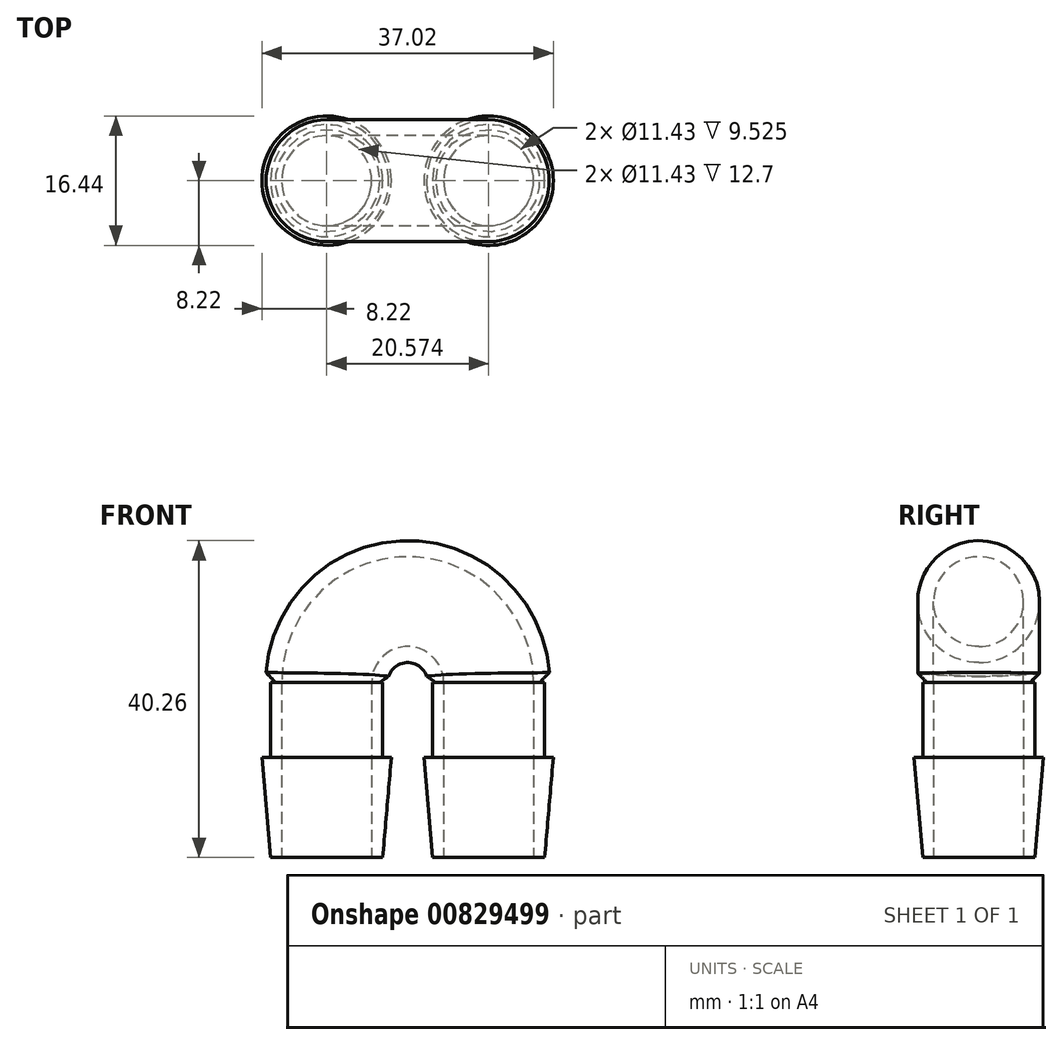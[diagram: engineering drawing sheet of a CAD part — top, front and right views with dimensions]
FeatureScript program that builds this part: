
annotation { "Feature Type Name" : "Feature", "Feature Type Description" : "" }
export const myFeature = defineFeature(function(context is Context, id is Id, definition is map)
    precondition{}
    {
        {
            var Q0;
            Q0=qCreatedBy(makeId("Top.planeOp"),FACE);
            var sketch = newSketch(context, id + "F0", { "sketchPlane" : qUnion([Q0])});
            skCircle(sketch, "E0", {"center": v(0, 0) * mm, "radius": 7.11 * mm});
            skCircle(sketch, "E1", {"center": v(20.57, 0) * mm, "radius": 7.11 * mm});
            skCircle(sketch, "E2", {"center": v(0, 0) * mm, "radius": 5.72 * mm});
            skCircle(sketch, "E3", {"center": v(20.57, 0) * mm, "radius": 5.72 * mm});
            skSolve(sketch);
        }
        {
            var Q0;
            Q0=makeQuery(id+"F0.imprint","IMPRINT",FACE,{"disambiguationData":[TD([[makeQuery(id+"F0.imprint","IMPRINT",EDGE,{"derivedFrom":sQuery(id+"F0.wireOp",EDGE,"E0")}),1.0]])]});
            var Q1;
            Q1=makeQuery(id+"F0.imprint","IMPRINT",FACE,{"disambiguationData":[TD([[makeQuery(id+"F0.imprint","IMPRINT",EDGE,{"derivedFrom":sQuery(id+"F0.wireOp",EDGE,"E2")}),1.0]])]});
            var Q2;
            Q2=makeQuery(id+"F0.imprint","IMPRINT",FACE,{"disambiguationData":[TD([[makeQuery(id+"F0.imprint","IMPRINT",EDGE,{"derivedFrom":sQuery(id+"F0.wireOp",EDGE,"E3")}),1.0]])]});
            var Q3;
            Q3=makeQuery(id+"F0.imprint","IMPRINT",FACE,{"disambiguationData":[TD([[makeQuery(id+"F0.imprint","IMPRINT",EDGE,{"derivedFrom":sQuery(id+"F0.wireOp",EDGE,"E1")}),1.0]])]});
            extrude(context, id + "F1", {"entities" : qUnion([Q0, Q1, Q2, Q3]), "depth" : 12.7 * mm, "offsetDistance" : 25.4 * mm, "hasDraft" : true, "draftAngle" : 5 * degree});
        }
        {
            var Q0;
            Q0=makeQuery(id+"F1.opExtrude","CAP_FACE",FACE,{"disambiguationData":[OSD([sQuery(id+"F0.wireOp",EDGE,"E0")])],"isStart":false});
            var sketch = newSketch(context, id + "F2", { "sketchPlane" : qUnion([Q0])});
            skCircle(sketch, "E4", {"center": v(0, 0) * mm, "radius": 7.11 * mm});
            skCircle(sketch, "E5", {"center": v(20.57, 0) * mm, "radius": 7.11 * mm});
            skCircle(sketch, "E6", {"center": v(0, 0) * mm, "radius": 5.72 * mm});
            skCircle(sketch, "E7", {"center": v(20.57, 0) * mm, "radius": 5.72 * mm});
            skSolve(sketch);
        }
        {
            var Q0;
            Q0=makeQuery(id+"F2.imprint","IMPRINT",FACE,{"disambiguationData":[TD([[makeQuery(id+"F2.imprint","IMPRINT",EDGE,{"derivedFrom":sQuery(id+"F2.wireOp",EDGE,"E4")}),1.0]])]});
            var Q1;
            Q1=makeQuery(id+"F2.imprint","IMPRINT",FACE,{"disambiguationData":[TD([[makeQuery(id+"F2.imprint","IMPRINT",EDGE,{"derivedFrom":sQuery(id+"F2.wireOp",EDGE,"E5")}),1.0]])]});
            extrude(context, id + "F3", {"entities" : qUnion([Q0, Q1]), "depth" : 9.52 * mm, "offsetDistance" : 25.4 * mm});
        }
        {
            var Q0;
            Q0=makeQuery(id+"F3.opExtrude","CAP_FACE",FACE,{"disambiguationData":[OSD([sQuery(id+"F2.wireOp",EDGE,"E5"),sQuery(id+"F2.wireOp",EDGE,"E7")])],"isStart":false});
            var sketch = newSketch(context, id + "F4", { "sketchPlane" : qUnion([Q0])});
            skLineSegment(sketch, "E8", {"start": v(0, 0) * mm, "end": v(20.57, 0) * mm});
            skLineSegment(sketch, "E9", {"start": v(10.29, 0) * mm, "end": v(10.29, 12.65) * mm});
            skCircle(sketch, "E10", {"center": v(0, 0) * mm, "radius": 5.72 * mm});
            skCircle(sketch, "E11", {"center": v(0, 0) * mm, "radius": 7.75 * mm});
            skSolve(sketch);
        }
        {
            var Q0;
            Q0=makeQuery(id+"F4.imprint","IMPRINT",FACE,{"disambiguationData":[TD([[makeQuery(id+"F4.imprint","IMPRINT",EDGE,{"derivedFrom":sQuery(id+"F4.wireOp",EDGE,"E10")}),-1.0]])]});
            var Q1;
            Q1=sQuery(id+"F4.wireOp",EDGE,"E9");
            revolve(context, id + "F5", {"surfaceOperationType" : NewSurfaceOperationType.NEW, "entities" : qUnion([Q0]), "axis" : qUnion([Q1]), "revolveType" : RevolveType.ONE_DIRECTION, "angle" : 180 * degree});
        }
        {
            var Q0;
            Q0=makeQuery(id+"F0.imprint","IMPRINT",FACE,{"disambiguationData":[TD([[makeQuery(id+"F0.imprint","IMPRINT",EDGE,{"derivedFrom":sQuery(id+"F0.wireOp",EDGE,"E2")}),1.0]])]});
            var Q1;
            Q1=makeQuery(id+"F1.opExtrude","CAP_FACE",FACE,{"disambiguationData":[OSD([sQuery(id+"F0.wireOp",EDGE,"E1")])],"isStart":false});
            extrude(context, id + "F6", {"entities" : qUnion([Q0]), "operationType" : NewBodyOperationType.REMOVE, "endBound" : BoundingType.UP_TO_SURFACE, "depth" : 25.4 * mm, "endBoundEntityFace" : qUnion([Q1]), "offsetDistance" : 25.4 * mm});
        }
        {
            var Q0;
            Q0=makeQuery(id+"F0.imprint","IMPRINT",FACE,{"disambiguationData":[TD([[makeQuery(id+"F0.imprint","IMPRINT",EDGE,{"derivedFrom":sQuery(id+"F0.wireOp",EDGE,"E3")}),1.0]])]});
            extrude(context, id + "F7", {"entities" : qUnion([Q0]), "operationType" : NewBodyOperationType.REMOVE, "endBound" : BoundingType.UP_TO_NEXT, "depth" : 25.4 * mm, "offsetDistance" : 25.4 * mm});
        }
        {
            var Q0;
            Q0=makeQuery(id+"F5.opRevolve","CAP_EDGE",EDGE,{"disambiguationData":[OSD([sQuery(id+"F4.wireOp",EDGE,"E11")])],"isStart":true});
            var Q1;
            Q1=makeQuery(id+"F5.opRevolve","CAP_EDGE",EDGE,{"disambiguationData":[OSD([sQuery(id+"F4.wireOp",EDGE,"E11")])],"isStart":false});
            chamfer(context, id + "F8", {"entities" : qUnion([Q0, Q1]), "width" : 1.27 * mm, "tangentPropagation" : true});
        }
    });
